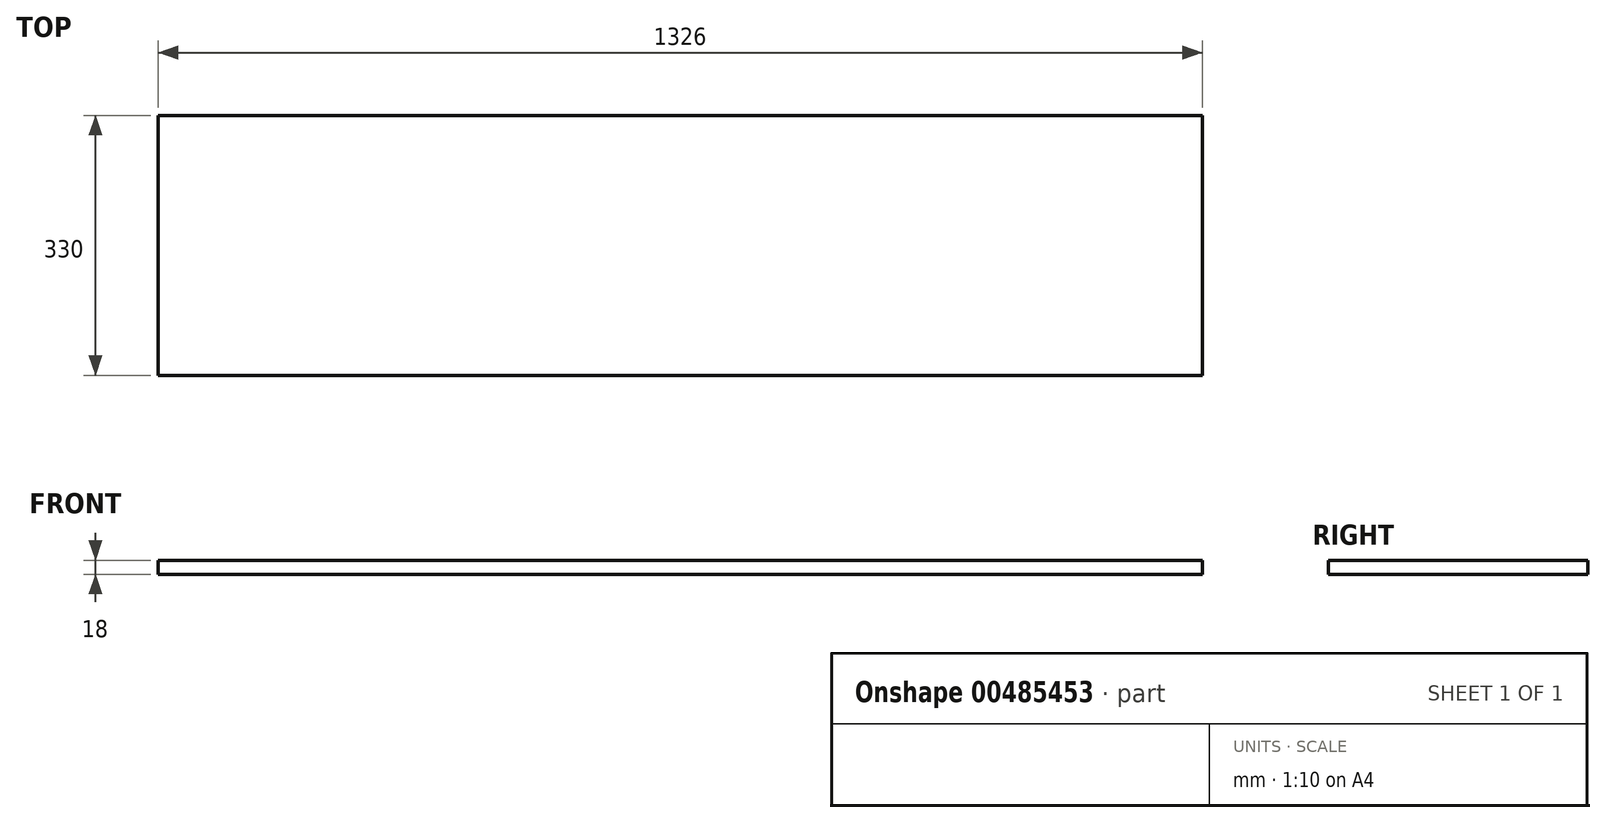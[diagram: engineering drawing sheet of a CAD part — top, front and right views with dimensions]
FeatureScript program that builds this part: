
annotation { "Feature Type Name" : "Feature", "Feature Type Description" : "" }
export const myFeature = defineFeature(function(context is Context, id is Id, definition is map)
    precondition{}
    {
        {
            var Q0;
            Q0=qCreatedBy(makeId("Top.planeOp"),FACE);
            var sketch = newSketch(context, id + "F0", { "sketchPlane" : qUnion([Q0])});
            skLineSegment(sketch, "E0.bottom", {"start": v(663, 165) * mm, "end": v(-663, 165) * mm});
            skLineSegment(sketch, "E0.top", {"start": v(663, -165) * mm, "end": v(-663, -165) * mm});
            skLineSegment(sketch, "E0.left", {"start": v(663, 165) * mm, "end": v(663, -165) * mm});
            skLineSegment(sketch, "E0.right", {"start": v(-663, 165) * mm, "end": v(-663, -165) * mm});
            skPoint(sketch, "E0.middle", {"position": v(0, 0) * mm});
            skSolve(sketch);
        }
        {
            var Q0;
            Q0 = qSketchRegion(id + "F0", true);
            extrude(context, id + "F1", {"entities" : qUnion([Q0]), "depth" : 18 * mm});
        }
    });
